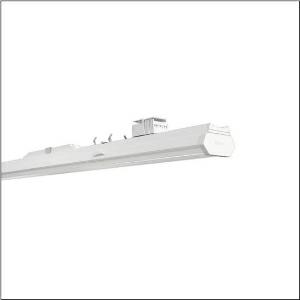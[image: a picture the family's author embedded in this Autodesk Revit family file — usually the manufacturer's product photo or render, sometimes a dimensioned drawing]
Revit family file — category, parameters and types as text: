
# Revit family: licross_r__21_protected_ho_52tp11mn4fxs_3689
name_source: partatom
category: Lighting Fixtures
units: mm (PartAtom-declared; Revit-internal decimal feet)

## family parameters
Cut with Voids When Loaded = No
Host = Face
Light Source = No
Part Type = Normal
Room Calculation Point = No
Round Connector Dimension = Use Diameter
Shared = No

## types (1)
- --- (1 x LED, 15020 lm, 83.2 W, 4000K)
    Apparent Load = 83 VA
    CIE Flux Codes = 84 94 98 99 100
    Color Rendering = 80
    Color Temperature = 4000K
    Default Elevation = 1800 mm
    Description = Licross® 21 Protected HO, luminaire insert, of sheet steel, galvanised, coil coated, white, length: 1.500mm, width: 66mm, height: 67mm, LED rated luminous flux: 15.020lm, light colour: 840, control gear: ON/OFF Multilumen, with plug, 3-pole, with phase selection, mains connection: 220..240V, AC, 50/60Hz, rated input power: 83W, halogen-free wiring, primary light control with lens, of plastic, primary optical cover: cover, of PMMA, light emission: direct distribution, primary light characteristic: symmetric, protection rating (complete): IP64, insulation class (complete): insulation class I (protective earthing), certification: CE, ENEC, VDE, UKCA, protection symbol: D if used in an environment with conductive dust loads with corresponding accessories, impact resistance: IK06, permissible ambient temperature for indoor applications: -35..+35°C, corresponds to IFS (International Featured Standards) requirements for safety and quality in the food industry, reducing of maximum allowable ambient temperature of 5°C with ceiling mounting, LABS conformity tested according to VDMA 24364:2018-05, packaging unit: 1 piece
    Height = 92 mm
    Lamp = 1 x LED
    Lamp Light Flux = 15020 lm
    Lamp Power = 83.2 W
    Lamp count = 1
    Length = 1500 mm
    Luminous efficacy = 181 lm/W
    Manufacturer = Siteco
    ModVariant = No
    Model = 52TP11MN4FXS
    Mounting Place = Ceiling
    Mounting Type = Pendant
    Number of Poles = 1
    OnlyDefault = Yes
    Power Factor = 1
    Product Name = Licross® 21 Protected HO
    Product group = luminaire insert
    ProductGroupID = 902
    Protection Class = Protection class I
    Protection Degree = IP 64
    RLX_Detail_Level = 1
    RLX_Emergency_Light_Flux = 0 lm
    RLX_Emergency_Type = 0
    RLX_Emergency_Type_DB = No
    RlxData = <blob elided: 21905 chars, md5=e55a27c3>
    Socket = socket
    Standby Power = 0 W
    System Light Flux = 15020 lm
    System Power = 83 W
    Type Comments = factory setting: luminous flux: 100 % | (A | C | E) | 195 mA
    Type Image = l_1256148.jpg
    URL = http://relux.com
    VarID = @adj_109094
    Voltage = 0 V
    Weight = 0.00 kg
    Width = 88 mm

## geometry (parser evidence)
native form markers: Blend x4, Sweep x9
no freeform markers — native parametric forms only
